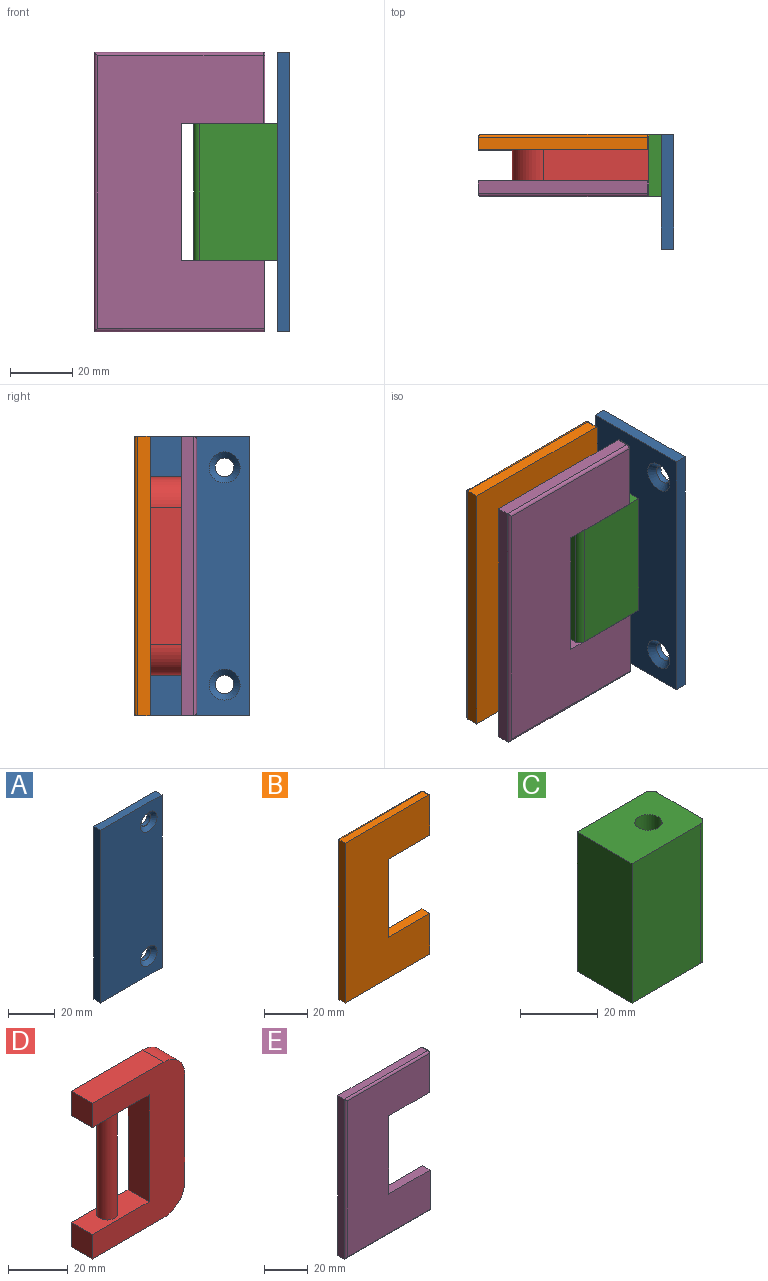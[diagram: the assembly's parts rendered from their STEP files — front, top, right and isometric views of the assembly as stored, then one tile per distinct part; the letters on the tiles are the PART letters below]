
ASSEMBLY  parts=5 mates=4
PART A: 10 faces, bbox 37x4x90 mm
  f0: plane 37x4mm, normal (0,0,1), area 148mm2, adj f1,f5,f6,f7
  f1: plane 90x4mm, normal (-1,0,0), area 360mm2, adj f0,f2,f6,f7
  f2: plane 37x4mm, normal (0,0,-1), area 148mm2, adj f1,f5,f6,f7
  f3: cylinder r=3mm len=6mm, axis (0,1,0), area 37.7mm2, adj f7,f9
  f4: cylinder r=3mm len=6mm, axis (0,1,0), area 37.7mm2, adj f7,f8
  f5: plane 90x4mm, normal (1,0,0), area 360mm2, adj f0,f2,f6,f7
  f6: plane 90x37mm, normal (0,-1,0), area 3172.9mm2, adj f0,f1,f2,f5,f8,f9
  f7: plane 90x37mm, normal (0,1,0), area 3273.5mm2, adj f0,f1,f2,f3,f4,f5
  f8: cone r=3mm half-angle=45deg, axis (0,-1,0), area 71.1mm2, adj f4,f6
  f9: cone r=3mm half-angle=45deg, axis (0,-1,0), area 71.1mm2, adj f3,f6
PART B: 16 faces, bbox 55x5.1x90.1 mm
  f0: plane 90x4mm, normal (-1,0,0), area 360mm2, adj f1,f7,f9,f11
  f1: plane 55x4mm, normal (0,0,-1), area 220mm2, adj f0,f2,f9,f12
  f2: plane 23x5mm, normal (1,0,0), area 114.8mm2, adj f1,f3,f8,f9,f12
  f3: plane 27x5mm, normal (0,0,1), area 135mm2, adj f2,f4,f8,f9
  f4: plane 44x5mm, normal (1,0,0), area 220mm2, adj f3,f5,f8,f9
  f5: plane 27x5mm, normal (0,0,-1), area 134.9mm2, adj f4,f6,f8,f9,f13
  f6: plane 22.5x4.5mm, normal (1,0,0), area 101.2mm2, adj f5,f9,f13,f14,f15
  f7: plane 54.5x4mm, normal (0,0,1), area 218mm2, adj f0,f9,f10,f15
  f8: plane 88x54mm, normal (0,1,0), area 3553mm2, adj f2,f3,f4,f5,f10,f11,f12,f13
  f9: plane 90x55mm, normal (0,-1,0), area 3761.9mm2, adj f0,f1,f2,f3,f4,f5,f6,f7
  f10: cylinder r=1mm len=54.5mm, axis (1,0,0), area 85mm2, adj f7,f8,f11,f14
  f11: cylinder r=1mm len=90mm, axis (0,0,1), area 140.2mm2, adj f0,f8,f10,f12
  f12: cylinder r=1mm len=55mm, axis (-1,0,0), area 85.8mm2, adj f1,f2,f8,f11
  f13: cylinder r=0.5mm len=22mm, axis (0,0,-1), area 17.3mm2, adj f5,f6,f8,f14
  f14: torus R=0.5mm, axis (-1,0,0), area 1mm2, adj f6,f10,f13,f15
  f15: cylinder r=0.5mm len=4mm, axis (0,1,0), area 3.1mm2, adj f6,f7,f9,f14
PART C: 9 faces, bbox 27x20x44 mm
  f0: plane 44x25mm, normal (0,1,0), area 1100mm2, adj f1,f5,f7,f8
  f1: plane 44x20mm, normal (-1,0,0), area 880mm2, adj f0,f2,f7,f8
  f2: plane 44x25mm, normal (0,-1,0), area 1100mm2, adj f1,f3,f7,f8
  f3: cylinder r=2mm len=44mm, axis (0,0,-1), area 138.2mm2, adj f2,f4,f7,f8
  f4: plane 44x16mm, normal (1,0,0), area 704mm2, adj f3,f5,f7,f8
  f5: cylinder r=2mm len=44mm, axis (0,0,-1), area 138.2mm2, adj f0,f4,f7,f8
  f6: cylinder r=3.5mm len=44mm, axis (0,0,-1), area 967.6mm2, adj f7,f8
  f7: plane 27x20mm, normal (0,0,1), area 499.8mm2, adj f0,f1,f2,f3,f4,f5,f6
  f8: plane 27x20mm, normal (0,0,-1), area 499.8mm2, adj f0,f1,f2,f3,f4,f5,f6
PART D: 13 faces, bbox 44x10x64 mm
  f0: plane 27x10mm, normal (0,0,-1), area 231.5mm2, adj f1,f9,f10,f11,f12
  f1: plane 44x10mm, normal (-1,0,0), area 440mm2, adj f0,f2,f10,f11
  f2: plane 27x10mm, normal (0,0,1), area 231.5mm2, adj f1,f3,f10,f11,f12
  f3: plane 10x10mm, normal (-1,0,0), area 100mm2, adj f2,f4,f10,f11
  f4: plane 34x10mm, normal (0,0,-1), area 340mm2, adj f3,f5,f10,f11
  f5: cylinder r=10mm len=10mm, axis (0,1,0), area 157.1mm2, adj f4,f6,f10,f11
  f6: plane 44x10mm, normal (1,0,0), area 440mm2, adj f5,f7,f10,f11
  f7: cylinder r=10mm len=10mm, axis (0,1,0), area 157.1mm2, adj f6,f8,f10,f11
  f8: plane 34x10mm, normal (0,0,1), area 340mm2, adj f7,f9,f10,f11
  f9: plane 10x10mm, normal (-1,0,0), area 100mm2, adj f0,f8,f10,f11
  f10: plane 64x44mm, normal (0,-1,0), area 1585.1mm2, adj f0,f1,f2,f3,f4,f5,f6,f7
  f11: plane 64x44mm, normal (0,1,0), area 1585.1mm2, adj f0,f1,f2,f3,f4,f5,f6,f7
  f12: cylinder r=3.5mm len=44mm, axis (0,0,-1), area 967.6mm2, adj f0,f2
PART E: 16 faces, bbox 55x5.1x90.1 mm
  f0: plane 90x4mm, normal (-1,0,0), area 360mm2, adj f1,f7,f9,f11
  f1: plane 55x4mm, normal (0,0,-1), area 220mm2, adj f0,f2,f9,f12
  f2: plane 23x5mm, normal (1,0,0), area 114.8mm2, adj f1,f3,f8,f9,f12
  f3: plane 27x5mm, normal (0,0,1), area 135mm2, adj f2,f4,f8,f9
  f4: plane 44x5mm, normal (1,0,0), area 220mm2, adj f3,f5,f8,f9
  f5: plane 27x5mm, normal (0,0,-1), area 134.9mm2, adj f4,f6,f8,f9,f13
  f6: plane 22.5x4.5mm, normal (1,0,0), area 101.2mm2, adj f5,f9,f13,f14,f15
  f7: plane 54.5x4mm, normal (0,0,1), area 218mm2, adj f0,f9,f10,f15
  f8: plane 88x54mm, normal (0,-1,0), area 3553mm2, adj f2,f3,f4,f5,f10,f11,f12,f13
  f9: plane 90x55mm, normal (0,1,0), area 3761.9mm2, adj f0,f1,f2,f3,f4,f5,f6,f7
  f10: cylinder r=1mm len=54.5mm, axis (1,0,0), area 85mm2, adj f7,f8,f11,f14
  f11: cylinder r=1mm len=90mm, axis (0,0,1), area 140.2mm2, adj f0,f8,f10,f12
  f12: cylinder r=1mm len=55mm, axis (-1,0,0), area 85.8mm2, adj f1,f2,f8,f11
  f13: cylinder r=0.5mm len=22mm, axis (0,0,-1), area 17.3mm2, adj f5,f6,f8,f14
  f14: torus R=0.5mm, axis (-1,0,0), area 1mm2, adj f6,f10,f13,f15
  f15: cylinder r=0.5mm len=4mm, axis (0,-1,0), area 3.1mm2, adj f6,f7,f9,f14
PLACE A rot(axis=(0,0,-1),90deg) t=(25.06,13.67,10.39)mm
PLACE B rot(axis=(0.03,0,1),0deg) t=(-37.94,3.67,-34.61)mm
PLACE C rot(axis=(0,0,1),180deg) t=(21.06,3.67,-11.61)mm
PLACE D rot(axis=(0,0,1),180deg) t=(17.06,3.67,-21.61)mm
PLACE E rot(axis=(0.03,0,1),0deg) t=(-37.94,3.67,-34.61)mm
MATE revolute D.f12 <-> C.f6  axis (0,0,-1) through (5.06,3.67,32.39)mm
MATE fastened E.f5 <-> D.f0  axis (0,0,1) through (17.06,-1.33,32.39)mm
MATE fastened C.f1 <-> A.f6  axis (1,0,0) through (21.06,13.67,10.39)mm
MATE fastened B.f5 <-> D.f0  axis (0,0,1) through (17.06,8.67,32.39)mm
